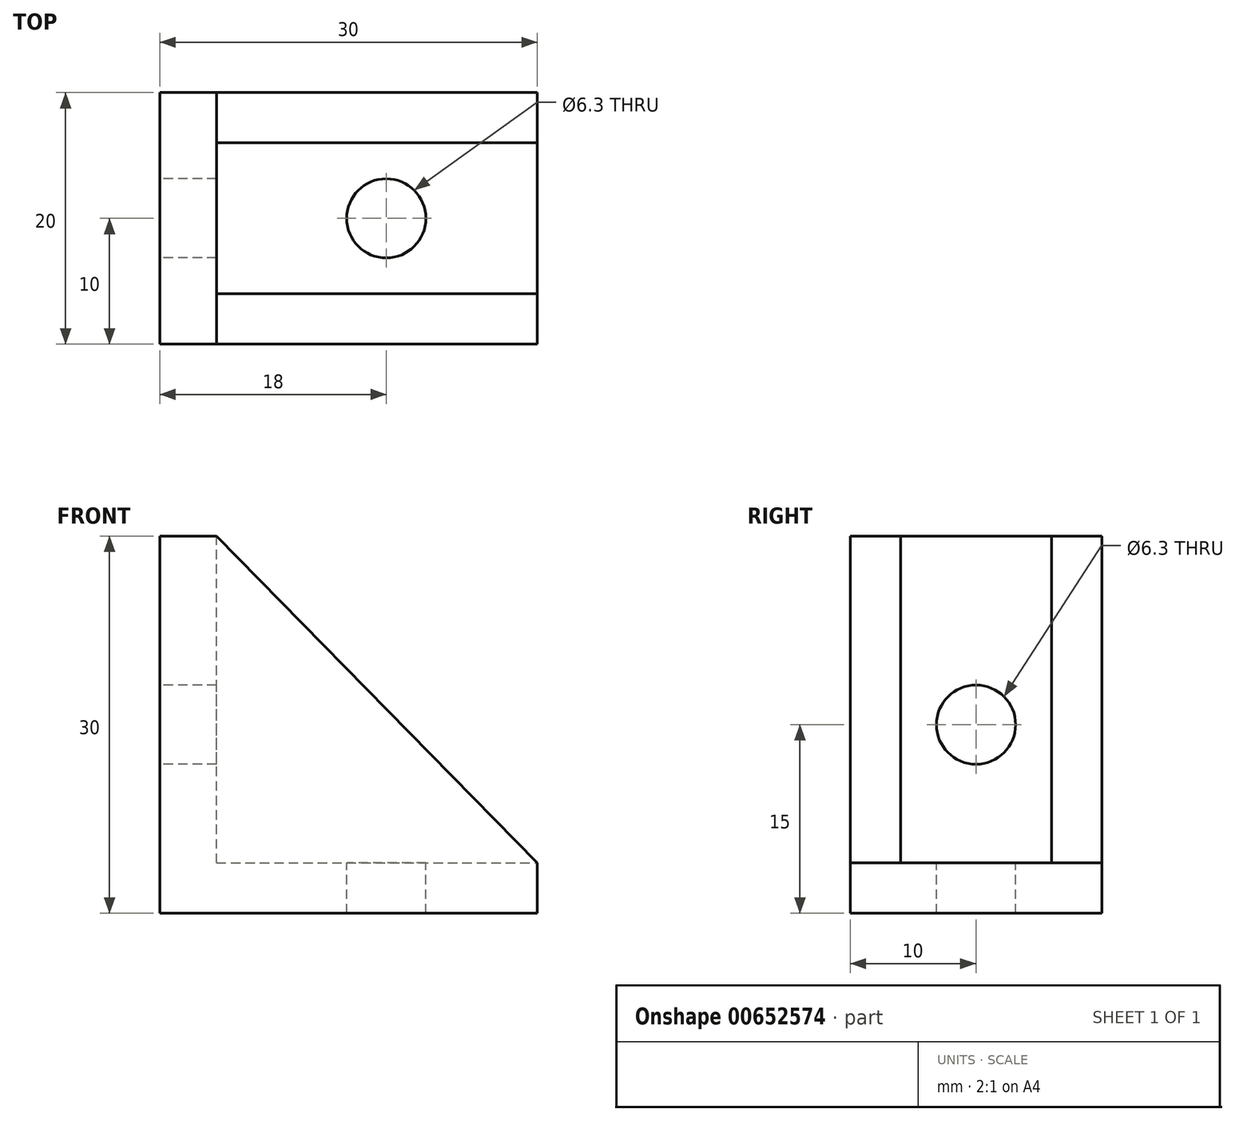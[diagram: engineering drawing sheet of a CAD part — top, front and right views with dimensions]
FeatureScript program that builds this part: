
annotation { "Feature Type Name" : "Feature", "Feature Type Description" : "" }
export const myFeature = defineFeature(function(context is Context, id is Id, definition is map)
    precondition{}
    {
        {
            var Q0;
            Q0=qCreatedBy(makeId("Front.planeOp"),FACE);
            var sketch = newSketch(context, id + "F0", { "sketchPlane" : qUnion([Q0])});
            skLineSegment(sketch, "E0.bottom", {"start": v(0, 0) * mm, "end": v(30, 0) * mm});
            skLineSegment(sketch, "E0.top", {"start": v(0, 30) * mm, "end": v(30, 30) * mm});
            skLineSegment(sketch, "E0.left", {"start": v(0, 0) * mm, "end": v(0, 30) * mm});
            skLineSegment(sketch, "E0.right", {"start": v(30, 0) * mm, "end": v(30, 30) * mm});
            skLineSegment(sketch, "E1", {"start": v(4.5, 30) * mm, "end": v(30, 4) * mm});
            skSolve(sketch);
        }
        {
            var Q0;
            {var subQ1=sQuery(id+"F0.wireOp",EDGE,"E0.bottom");Q0=makeQuery(id+"F0.imprint","IMPRINT",FACE,{"disambiguationData":[TD([[makeQuery(id+"F0.imprint","IMPRINT",EDGE,{"derivedFrom":subQ1}),1.0]])]});}
            extrude(context, id + "F1", {"entities" : qUnion([Q0]), "depth" : 20 * mm, "offsetDistance" : 25 * mm});
        }
        {
            var Q0;
            Q0=makeQuery(id+"F1.opExtrude","SWEPT_FACE",FACE,{"disambiguationData":[OSD([sQuery(id+"F0.wireOp",EDGE,"E0.top")])]});
            var sketch = newSketch(context, id + "F2", { "sketchPlane" : qUnion([Q0])});
            skLineSegment(sketch, "E2.bottom", {"start": v(4.5, -4) * mm, "end": v(30, -4) * mm});
            skLineSegment(sketch, "E2.top", {"start": v(4.5, -16) * mm, "end": v(30, -16) * mm});
            skLineSegment(sketch, "E2.left", {"start": v(4.5, -4) * mm, "end": v(4.5, -16) * mm});
            skLineSegment(sketch, "E2.right", {"start": v(30, -4) * mm, "end": v(30, -16) * mm});
            skSolve(sketch);
        }
        {
            var Q0;
            Q0 = qSketchRegion(id + "F2", true);
            extrude(context, id + "F3", {"entities" : qUnion([Q0]), "operationType" : NewBodyOperationType.REMOVE, "oppositeDirection" : true, "depth" : (30 - 4) * mm, "offsetDistance" : 25 * mm});
        }
        {
            var Q0;
            Q0=qCreatedBy(makeId("Right.planeOp"),FACE);
            var sketch = newSketch(context, id + "F4", { "sketchPlane" : qUnion([Q0])});
            skCircle(sketch, "E3", {"center": v(-10, 15) * mm, "radius": 3.15 * mm});
            skSolve(sketch);
        }
        {
            var Q0;
            Q0 = qSketchRegion(id + "F4", true);
            extrude(context, id + "F5", {"entities" : qUnion([Q0]), "operationType" : NewBodyOperationType.REMOVE, "depth" : 25 * mm, "offsetDistance" : 25 * mm});
        }
        {
            var Q0;
            Q0=makeQuery(id+"F3.boolean.opBoolean","COPY",FACE,{"derivedFrom":makeQuery(id+"F3.opExtrude","CAP_FACE",FACE,{"disambiguationData":[OSD([sQuery(id+"F2.wireOp",EDGE,"E2.bottom"),sQuery(id+"F2.wireOp",EDGE,"E2.top"),sQuery(id+"F2.wireOp",EDGE,"E2.left"),sQuery(id+"F2.wireOp",EDGE,"E2.right")])],"isStart":false})});
            var sketch = newSketch(context, id + "F6", { "sketchPlane" : qUnion([Q0])});
            skCircle(sketch, "E4", {"center": v(18, -10) * mm, "radius": 3.15 * mm});
            skSolve(sketch);
        }
        {
            var Q0;
            Q0 = qSketchRegion(id + "F6", true);
            extrude(context, id + "F7", {"entities" : qUnion([Q0]), "operationType" : NewBodyOperationType.REMOVE, "oppositeDirection" : true, "depth" : 25 * mm, "offsetDistance" : 25 * mm});
        }
    });
